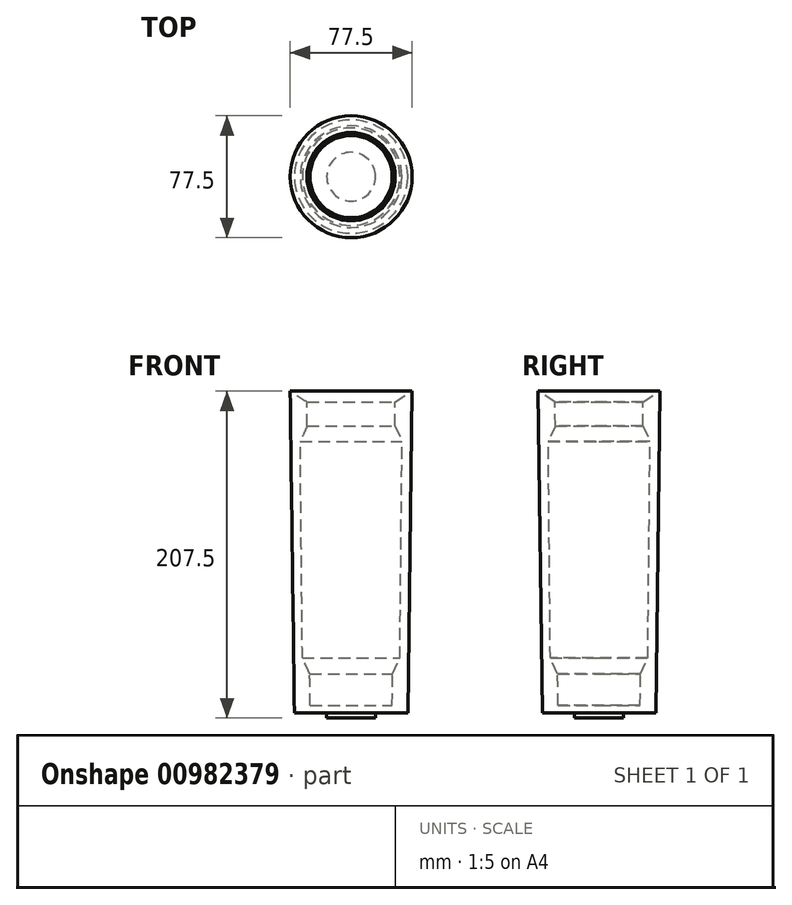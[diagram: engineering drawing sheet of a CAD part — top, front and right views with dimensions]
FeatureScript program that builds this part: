
annotation { "Feature Type Name" : "Feature", "Feature Type Description" : "" }
export const myFeature = defineFeature(function(context is Context, id is Id, definition is map)
    precondition{}
    {
        {
            var Q0;
            Q0=qCreatedBy(makeId("Front.planeOp"),FACE);
            var sketch = newSketch(context, id + "F0", { "sketchPlane" : qUnion([Q0])});
            skLineSegment(sketch, "E0", {"start": v(28, 0) * mm, "end": v(28, 12.5) * mm});
            skLineSegment(sketch, "E1", {"start": v(28, 12.5) * mm, "end": v(45.25, 12.5) * mm});
            skLineSegment(sketch, "E2", {"start": v(45.25, 12.5) * mm, "end": v(45.25, 0) * mm});
            skLineSegment(sketch, "E3", {"start": v(45.25, 0) * mm, "end": v(38.75, 0) * mm});
            skLineSegment(sketch, "E4", {"start": v(38.75, 0) * mm, "end": v(38.75, -36.5) * mm});
            skLineSegment(sketch, "E5", {"start": v(38.75, -36.5) * mm, "end": v(28, -43.5) * mm});
            skLineSegment(sketch, "E6", {"start": v(28, -43.5) * mm, "end": v(28, 0) * mm});
            skLineSegment(sketch, "E7", {"start": v(15.5, -241) * mm, "end": v(36, -241) * mm});
            skLineSegment(sketch, "E8", {"start": v(36, -241) * mm, "end": v(38.75, -36.5) * mm});
            skLineSegment(sketch, "E9", {"start": v(0, -241) * mm, "end": v(0, -244) * mm});
            skLineSegment(sketch, "E10", {"start": v(15.5, -244) * mm, "end": v(15.5, -241) * mm});
            skLineSegment(sketch, "E11", {"start": v(0, -244) * mm, "end": v(15.5, -244) * mm});
            skLineSegment(sketch, "E12", {"start": v(0, -241) * mm, "end": v(0, -236) * mm});
            skLineSegment(sketch, "E13", {"start": v(0, -236) * mm, "end": v(26.1, -236) * mm});
            skLineSegment(sketch, "E14", {"start": v(28, -43.5) * mm, "end": v(27.85, -58.5) * mm});
            skLineSegment(sketch, "E15", {"start": v(26.3, -216) * mm, "end": v(30.96, -206) * mm});
            skLineSegment(sketch, "E16", {"start": v(30.96, -206) * mm, "end": v(32.32, -68.5) * mm});
            skLineSegment(sketch, "E17", {"start": v(32.32, -68.5) * mm, "end": v(27.85, -58.5) * mm});
            skLineSegment(sketch, "E18.trimOffspring", {"start": v(26.3, -216) * mm, "end": v(26.1, -236) * mm});
            skLineSegment(sketch, "E19", {"start": v(0, -236) * mm, "end": v(0, 0) * mm, "construction": true});
            skSolve(sketch);
        }
        {
            var Q0;
            Q0=makeQuery(id+"F0.imprint","IMPRINT",FACE,{"disambiguationData":[TD([[makeQuery(id+"F0.imprint","IMPRINT",EDGE,{"derivedFrom":sQuery(id+"F0.wireOp",EDGE,"E5")}),1.0]])]});
            var Q1;
            Q1=sQuery(id+"F0.wireOp",EDGE,"E19");
            revolve(context, id + "F1", {"surfaceOperationType" : NewSurfaceOperationType.NEW, "entities" : qUnion([Q0]), "axis" : qUnion([Q1]), "revolveType" : RevolveType.FULL});
        }
    });
